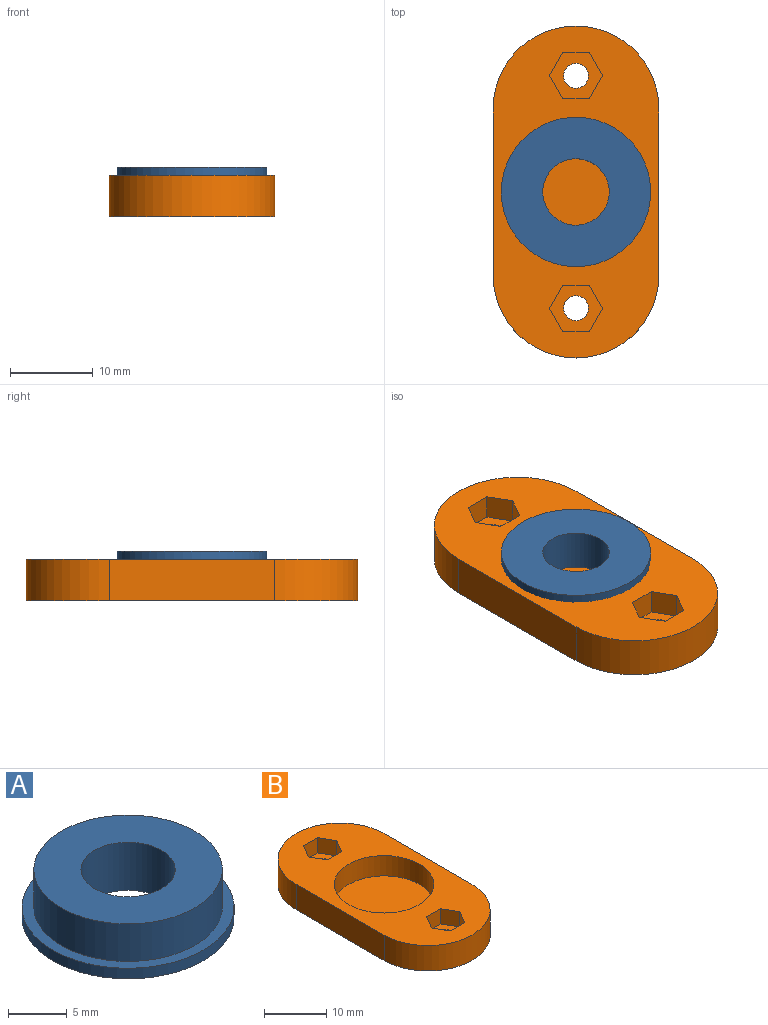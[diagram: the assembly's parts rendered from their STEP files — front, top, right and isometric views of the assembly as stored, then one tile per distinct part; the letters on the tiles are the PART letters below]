
ASSEMBLY  parts=2 mates=1
PART A: 6 faces, bbox 18x18x5 mm
  f0: cylinder r=9mm len=18mm, axis (0,0,-1), area 62.2mm2, adj f1,f2
  f1: plane 18x18mm, normal (0,0,1), area 53.4mm2, adj f0,f3
  f2: plane 18x18mm, normal (0,0,-1), area 204.2mm2, adj f0,f5
  f3: cylinder r=8mm len=16mm, axis (0,0,-1), area 196mm2, adj f1,f4
  f4: plane 16x16mm, normal (0,0,1), area 150.8mm2, adj f3,f5
  f5: cylinder r=4mm len=8mm, axis (0,0,1), area 125.7mm2, adj f2,f4
PART B: 24 faces, bbox 20x40x5 mm
  f0: plane 20x5mm, normal (1,0,0), area 100mm2, adj f2,f3,f6,f7
  f1: plane 20x5mm, normal (-1,0,0), area 100mm2, adj f2,f3,f6,f7
  f2: plane 40x20mm, normal (0,0,1), area 459.7mm2, adj f0,f1,f4,f6,f7,f8,f9,f10
  f3: plane 40x20mm, normal (0,0,-1), area 700mm2, adj f0,f1,f6,f7,f22,f23
  f4: cylinder r=8mm len=16mm, axis (0,0,1), area 201.1mm2, adj f2,f5
  f5: plane 16x16mm, normal (0,0,1), area 201.1mm2, adj f4
  f6: cylinder r=10mm len=20mm, axis (0,0,-1), area 157.1mm2, adj f0,f1,f2,f3
  f7: cylinder r=10mm len=20mm, axis (0,0,-1), area 157.1mm2, adj f0,f1,f2,f3
  f8: plane 3x2.78mm, normal (0.87,0.5,0), area 9.6mm2, adj f2,f9,f13,f14
  f9: plane 3.2x3mm, normal (0,1,0), area 9.6mm2, adj f2,f8,f10,f14
  f10: plane 3x2.78mm, normal (-0.87,0.5,0), area 9.6mm2, adj f2,f9,f11,f14
  f11: plane 3x2.78mm, normal (-0.87,-0.5,0), area 9.6mm2, adj f2,f10,f12,f14
  f12: plane 3.2x3mm, normal (0,-1,0), area 9.6mm2, adj f2,f11,f13,f14
  f13: plane 3x2.78mm, normal (0.87,-0.5,0), area 9.6mm2, adj f2,f8,f12,f14
  f14: plane 6.41x5.55mm, normal (0,0,1), area 19.6mm2, adj f8,f9,f10,f11,f12,f13,f23
  f15: plane 3x2.78mm, normal (-0.87,-0.5,0), area 9.6mm2, adj f2,f16,f20,f21
  f16: plane 3.2x3mm, normal (0,-1,0), area 9.6mm2, adj f2,f15,f17,f21
  f17: plane 3x2.78mm, normal (0.87,-0.5,0), area 9.6mm2, adj f2,f16,f18,f21
  f18: plane 3x2.78mm, normal (0.87,0.5,0), area 9.6mm2, adj f2,f17,f19,f21
  f19: plane 3.2x3mm, normal (0,1,0), area 9.6mm2, adj f2,f18,f20,f21
  f20: plane 3x2.78mm, normal (-0.87,0.5,0), area 9.6mm2, adj f2,f15,f19,f21
  f21: plane 6.41x5.55mm, normal (0,0,1), area 19.6mm2, adj f15,f16,f17,f18,f19,f20,f22
  f22: cylinder r=1.5mm len=3mm, axis (0,0,1), area 18.8mm2, adj f3,f21
  f23: cylinder r=1.5mm len=3mm, axis (0,0,1), area 18.8mm2, adj f3,f14
PLACE A rot(axis=(0,1,0),180deg) t=(-15.97,-5.71,8.77)mm
PLACE B t=(-15.97,-5.71,2.77)mm
MATE planar A.f3 <-> B.f4  axis (0,0,-1) through (-15.97,-5.71,3.77)mm
